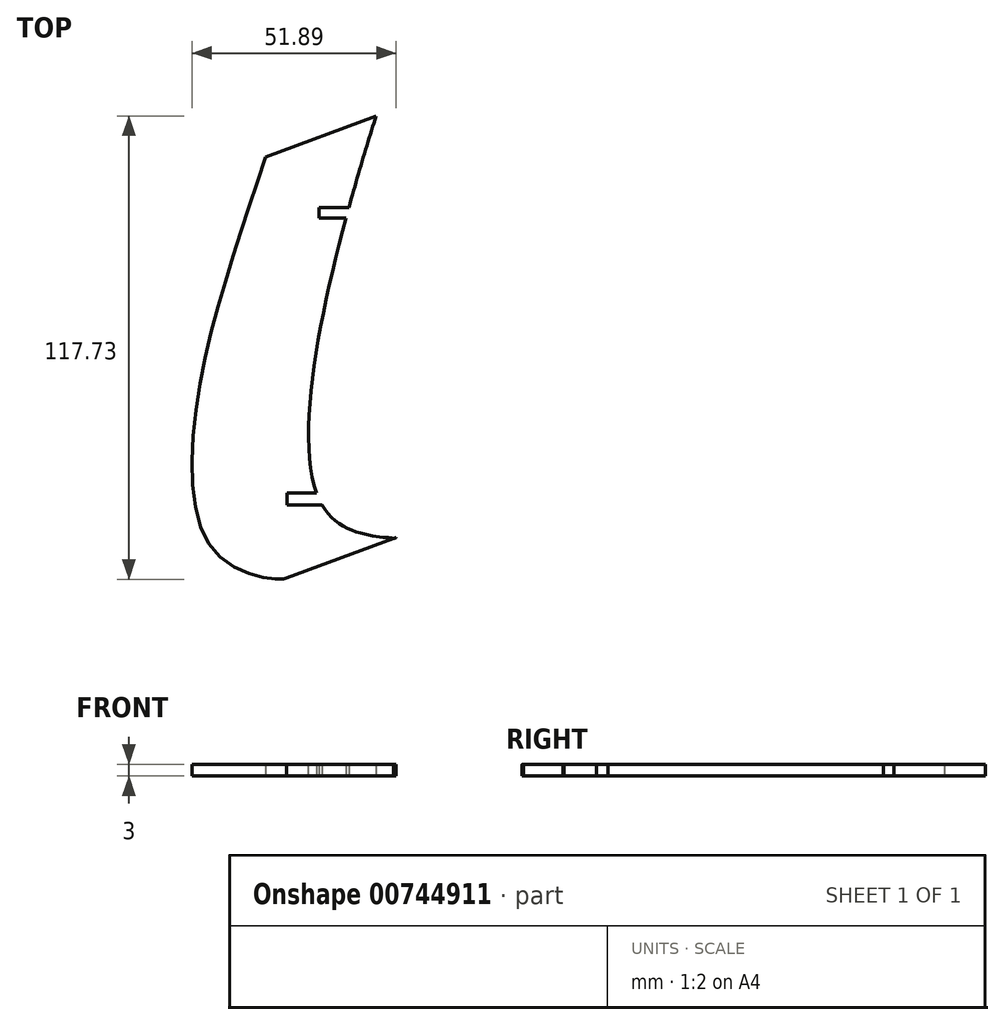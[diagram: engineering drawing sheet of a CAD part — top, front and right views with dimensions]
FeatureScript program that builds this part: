
annotation { "Feature Type Name" : "Feature", "Feature Type Description" : "" }
export const myFeature = defineFeature(function(context is Context, id is Id, definition is map)
    precondition{}
    {
        {
            var Q0;
            Q0=qCreatedBy(makeId("Top.planeOp"),FACE);
            var sketch = newSketch(context, id + "F0", { "sketchPlane" : qUnion([Q0])});
            skFitSpline(sketch, "E0", {"points": [v(-21.61, -53.98) * mm, v(-22.15, -54.25) * mm], "startDerivative": vector(-0.54, -0.27) * mm, "endDerivative": vector(-0.54, -0.27) * mm});
            skFitSpline(sketch, "E1", {"points": [v(-11.73, 58.6) * mm, v(-24.14, -42.23) * mm, v(-7.69, -48.7) * mm, v(-7.27, -48.77) * mm, v(-6.61, -48.43) * mm], "startDerivative": vector(-47.2, -148.39) * mm, "endDerivative": vector(-14.6, -1.04) * mm});
            skFitSpline(sketch, "E2", {"points": [v(-6.61, -48.43) * mm, v(-7.15, -48.7) * mm], "startDerivative": vector(-0.54, -0.27) * mm, "endDerivative": vector(-0.54, -0.27) * mm});
            skFitSpline(sketch, "E3", {"points": [v(-39.87, 48.2) * mm, v(-56.55, -10) * mm, v(-52.27, -52.63) * mm, v(-35.83, -59.1) * mm, v(-34.48, -58.83) * mm, v(-34.75, -58.83) * mm], "startDerivative": vector(-47.2, -148.39) * mm, "endDerivative": vector(-14.6, -1.04) * mm});
            skLineSegment(sketch, "E4", {"start": v(-39.87, 48.2) * mm, "end": v(-11.73, 58.6) * mm});
            skLineSegment(sketch, "E5", {"start": v(-34.48, -58.83) * mm, "end": v(-6.35, -48.41) * mm});
            skPoint(sketch, "E6", {"position": v(-27.27, -3.46) * mm});
            skSolve(sketch);
        }
        {
            var Q0;
            Q0 = qSketchRegion(id + "F0", true);
            extrude(context, id + "F1", {"entities" : qUnion([Q0]), "depth" : 3 * mm, "offsetDistance" : 25 * mm});
        }
        {
            var Q0;
            Q0=qCreatedBy(makeId("Top.planeOp"),FACE);
            var sketch = newSketch(context, id + "F2", { "sketchPlane" : qUnion([Q0])});
            skLineSegment(sketch, "E7.bottom", {"start": v(-26.22, 32.7) * mm, "end": v(-10.22, 32.7) * mm});
            skLineSegment(sketch, "E7.top", {"start": v(-26.22, 35.29) * mm, "end": v(-10.22, 35.29) * mm});
            skLineSegment(sketch, "E7.left", {"start": v(-26.22, 32.7) * mm, "end": v(-26.22, 35.29) * mm});
            skLineSegment(sketch, "E7.right", {"start": v(-10.22, 32.7) * mm, "end": v(-10.22, 35.29) * mm});
            skPoint(sketch, "E7.middle", {"position": v(-18.22, 34) * mm});
            skSolve(sketch);
        }
        {
            var Q0;
            Q0 = qSketchRegion(id + "F2", true);
            extrude(context, id + "F3", {"entities" : qUnion([Q0]), "operationType" : NewBodyOperationType.REMOVE, "depth" : 3 * mm, "offsetDistance" : 25 * mm});
        }
        {
            var Q0;
            Q0=qCreatedBy(makeId("Top.planeOp"),FACE);
            var sketch = newSketch(context, id + "F4", { "sketchPlane" : qUnion([Q0])});
            skLineSegment(sketch, "E8.bottom", {"start": v(-34.4, -40.26) * mm, "end": v(-18.4, -40.26) * mm});
            skLineSegment(sketch, "E8.top", {"start": v(-34.4, -37.26) * mm, "end": v(-18.4, -37.26) * mm});
            skLineSegment(sketch, "E8.left", {"start": v(-18.4, -40.26) * mm, "end": v(-18.4, -37.26) * mm});
            skLineSegment(sketch, "E8.right", {"start": v(-34.4, -40.26) * mm, "end": v(-34.4, -37.26) * mm});
            skPoint(sketch, "E8.middle", {"position": v(-26.4, -38.76) * mm});
            skSolve(sketch);
        }
        {
            var Q0;
            Q0 = qSketchRegion(id + "F4", true);
            extrude(context, id + "F5", {"entities" : qUnion([Q0]), "operationType" : NewBodyOperationType.REMOVE, "depth" : 3 * mm, "offsetDistance" : 25 * mm});
        }
    });
